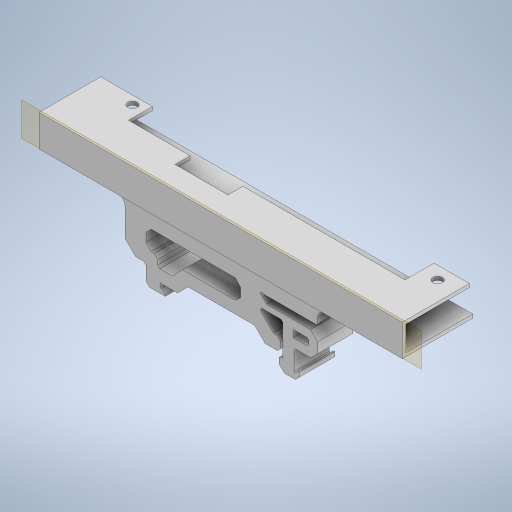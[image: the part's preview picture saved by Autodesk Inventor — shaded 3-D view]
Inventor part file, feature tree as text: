
AUTODESK INVENTOR PART (.ipt)
format: ipt  version: 2024 (Build 280153000, 153)  size: 466,432 bytes
history: native  units: in
note: dims shown in document units (in); Inventor stores cm internally (conversion verified against a paired STEP export)
features: extrude x5, sketch x2, fillet x2, plane x1
ambient origin geometry x8: Origin, YZ Plane, XZ Plane, XY Plane, X Axis, Y Axis, Z Axis, Center Point
bodies: Solid1 (feature_tree)
feature tree (10):
  sketch  "Sketch1"  dims[d0=0.1043in d1=0.1043in]
  extrude  "Extrusion1"  Depth=0.1043in
  extrude  "Extrusion2"  Depth=0.5768in
  extrude  "Extrusion3"  Depth=0.3937in
  extrude  "Extrusion4"  Depth=0.7087in
  plane  "Work Plane1"
  extrude  "Extrusion5"  Depth=0.6496in
  fillet  "Fillet1"  Radius=0.5541in
  fillet  "Fillet2"  Radius=0.4498in
  sketch  "Sketch5"  dims[d2=4.0591in d3=0.5768in d4=0.3937in d5=0.7087in d6=0.6496in d7=0.5541in d8=0.4498in d9=0.3839in d10=0.564in d11=0.2096in d12=0.0394in d13=0.0in d14=0.0394in d15=0.315in d16=0.0in d17=0.0394in d18=0.748in d19=0.0in d21=0.5906in d23=0.0787in d24=0.0in d26=0.2559in d28=1.811in d29=0.2362in d30=0.3758in d31=0.1566in d32=0.1762in d33=0.1957in d34=0.1387in d35=0.1174in d36=0.0391in d37=0.0157in d38=2.1217in d39=0.0973in d40=0.0587in d41=0.0587in d42=0.0548in d43=0.0235in d44=0.9395in d45=0.0587in d46=0.0973in d47=0.5854in d48=0.1174in d49=0.7438in d50=0.1174in d51=0.1174in d52=0.137in d53=0.1475in d54=0.0277in d55=0.2143in d56=0.3464in d57=0.0196in d58=0.0626in d59=0.0137in d60=0.0274in d61=0.0607in d62=0.1213in d63=0.047in d64=0.0509in d65=0.0157in d66=0.0356in d67=0.0094in d68=0.2063in d69=0.0196in d70=0.1664in d71=0.0783in d72=0.1174in d73=0.0783in d74=0.4893in d75=0.0783in d76=0.6302in d77=0.0156in d78=0.1253in d79=0.1174in d80=0.1174in d81=0.1174in d82=0.0391in d83=0.0391in d84=0.0391in d85=0.1475in d86=0.0695in d87=0.0391in d88=0.0391in d89=0.0196in d90=0.0196in d91=0.0196in d92=0.0196in d93=0.0196in d94=0.0658in d95=0.0235in d96=0.0587in d97=0.0391in d98=0.0391in d99=0.0391in d100=0.0626in d101=0.0548in d102=0.0156in d103=0.0471in d104=0.0607in d105=0.0137in d106=0.0196in d107=0.094in d108=0.0196in d109=0.0156in d110=0.1376in d111=0.0352in d112=0.2349in d113=0.1566in d114=0.3568in d115=0.1566in d116=0.0115in d117=0.0156in d118=0.0772in d119=0.1751in d120=0.0984in d121=0.118in d122=4.0591in d123=2.153in d124=0.953in d125=0.3937in d126=0.0in d127=0.0787in d128=0.0787in]
